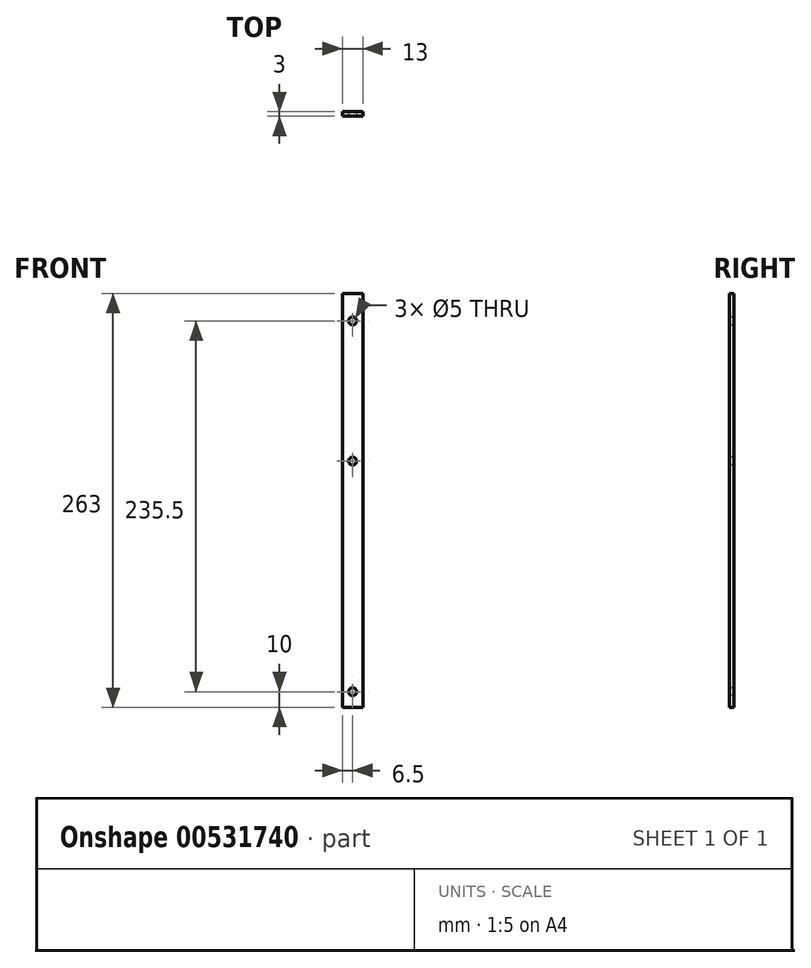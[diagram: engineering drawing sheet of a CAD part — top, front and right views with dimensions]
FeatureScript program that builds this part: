
annotation { "Feature Type Name" : "Feature", "Feature Type Description" : "" }
export const myFeature = defineFeature(function(context is Context, id is Id, definition is map)
    precondition{}
    {
        {
            var Q0;
            Q0=qCreatedBy(makeId("Front.planeOp"),FACE);
            var sketch = newSketch(context, id + "F0", { "sketchPlane" : qUnion([Q0])});
            skLineSegment(sketch, "E0.bottom", {"start": v(6.5, 131.5) * mm, "end": v(-6.5, 131.5) * mm});
            skLineSegment(sketch, "E0.top", {"start": v(6.5, -131.5) * mm, "end": v(-6.5, -131.5) * mm});
            skLineSegment(sketch, "E0.left", {"start": v(6.5, 131.5) * mm, "end": v(6.5, -131.5) * mm});
            skLineSegment(sketch, "E0.right", {"start": v(-6.5, 131.5) * mm, "end": v(-6.5, -131.5) * mm});
            skPoint(sketch, "E0.middle", {"position": v(0, 0) * mm});
            skSolve(sketch);
        }
        {
            var Q0;
            Q0=makeQuery(id+"F0.imprint","IMPRINT",FACE,{"disambiguationData":[TD([[makeQuery(id+"F0.imprint","IMPRINT",EDGE,{"derivedFrom":sQuery(id+"F0.wireOp",EDGE,"E0.bottom")}),1.0]])]});
            extrude(context, id + "F1", {"entities" : qUnion([Q0]), "depth" : 3 * mm, "offsetDistance" : 25 * mm});
        }
        {
            var Q0;
            Q0=makeQuery(id+"F1.opExtrude","CAP_FACE",FACE,{"disambiguationData":[OSD([sQuery(id+"F0.wireOp",EDGE,"E0.bottom"),sQuery(id+"F0.wireOp",EDGE,"E0.top"),sQuery(id+"F0.wireOp",EDGE,"E0.left"),sQuery(id+"F0.wireOp",EDGE,"E0.right")])],"isStart":false});
            var sketch = newSketch(context, id + "F2", { "sketchPlane" : qUnion([Q0])});
            skLineSegment(sketch, "E1", {"start": v(0, 131.5) * mm, "end": v(0, 114) * mm});
            skPoint(sketch, "E1.endSnap0", {"position": v(0, 131.5) * mm});
            skLineSegment(sketch, "E2", {"start": v(0, -131.5) * mm, "end": v(0, -121.5) * mm});
            skPoint(sketch, "E2.endSnap0", {"position": v(0, -131.5) * mm});
            skLineSegment(sketch, "E3", {"start": v(0, 131.5) * mm, "end": v(0, 31.5) * mm});
            skLineSegment(sketch, "E4", {"start": v(0, 31.5) * mm, "end": v(0, 25) * mm});
            skCircle(sketch, "E5", {"center": v(0, 114) * mm, "radius": 2.5 * mm});
            skCircle(sketch, "E6", {"center": v(0, 25) * mm, "radius": 2.5 * mm});
            skCircle(sketch, "E7", {"center": v(0, -121.5) * mm, "radius": 2.5 * mm});
            skSolve(sketch);
        }
        {
            var Q0;
            {var subQ0=sQuery(id+"F2.wireOp",EDGE,"E3");var subQ1=makeQuery(id+"F2.imprint","IMPRINT",VERTEX,{"derivedFrom":subQ0});Q0=makeQuery(id+"F2.imprint","IMPRINT",FACE,{"disambiguationData":[TD([[makeQuery(id+"F2.imprint","IMPRINT",EDGE,{"disambiguationData":[TD([[subQ1,1.0]])],"derivedFrom":subQ0}),-1.0]])]});}
            var Q1;
            {var subQ0=sQuery(id+"F2.wireOp",EDGE,"E3");var subQ1=makeQuery(id+"F2.imprint","IMPRINT",VERTEX,{"derivedFrom":subQ0});Q1=makeQuery(id+"F2.imprint","IMPRINT",FACE,{"disambiguationData":[TD([[makeQuery(id+"F2.imprint","IMPRINT",EDGE,{"disambiguationData":[TD([[subQ1,1.0]])],"derivedFrom":subQ0}),1.0]])]});}
            var Q2;
            Q2=makeQuery(id+"F2.imprint","IMPRINT",FACE,{"disambiguationData":[TD([[makeQuery(id+"F2.imprint","IMPRINT",EDGE,{"derivedFrom":sQuery(id+"F2.wireOp",EDGE,"E6")}),1.0]])]});
            var Q3;
            Q3=makeQuery(id+"F2.imprint","IMPRINT",FACE,{"disambiguationData":[TD([[makeQuery(id+"F2.imprint","IMPRINT",EDGE,{"derivedFrom":sQuery(id+"F2.wireOp",EDGE,"E7")}),1.0]])]});
            extrude(context, id + "F3", {"entities" : qUnion([Q0, Q1, Q2, Q3]), "operationType" : NewBodyOperationType.REMOVE, "oppositeDirection" : true, "depth" : 25 * mm, "offsetDistance" : 25 * mm});
        }
    });
